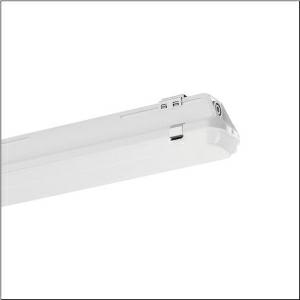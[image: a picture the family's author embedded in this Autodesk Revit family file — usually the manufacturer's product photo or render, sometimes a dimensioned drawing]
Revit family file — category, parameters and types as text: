
# Revit family: monsun_11_51fp107p4b0u
name_source: partatom
category: Lighting Fixtures
units: mm (PartAtom-declared; Revit-internal decimal feet)

## family parameters
Cut with Voids When Loaded = No
Host = Face
Light Source = No
Part Type = Normal
Room Calculation Point = No
Round Connector Dimension = Use Diameter
Shared = No

## types (1)
- Monsun 11 (1 x LED, 12070 lm, 62.4 W, 4000K)
    Apparent Load = 62 VA
    CIE Flux Codes = 47 76 93 94 100
    Color Rendering = 80
    Color Temperature = 4000K
    Default Elevation = 1800 mm
    Description = Monsun 11, damp-proof luminaire, chain hanger, primary optical cover: enclosure, of PMMA, light emission: direct distribution, primary light characteristic: symmetric, installation type: suspended mounting, surface-mounted, horizontal mounting, vertical mounting, LED, rated luminous flux: 12.070lm, luminous efficacy: 193lm/W, light colour: 840, colour temperature: 4000K, control gear: ON/OFF, with terminal, 3-pole, max. 2.5mm², mains connection: 220..240V, AC, 50/60Hz, rated input power: 62W, luminaire housing, of glass-fibre reinforced polyester, uncoated, bright grey, incl. chain hanger, length: 1.590mm, width: 90mm, height: 88mm, clip for enclosure, of stainless steel (V2A), ceiling mounting element, of stainless steel (V2A), chain hanger, of stainless steel (V2A), protection rating (complete): IP66, insulation class (complete): insulation class I (protective earthing), certification: CE, ENEC, VDE, UKCA, protection symbol: D, impact resistance: IK04, permissible operating ambient temperature: -35..+35°C, standard: EN 50419, EN 60598-2-1, contact your sales advisor before using the luminaires in applications with unclear chemical exposure, large temperature fluctuations or condensation-forming humidity, LABS conformity tested according to VDMA 24364:2018-05, no direct snow, no direct sun, no direct rain, for indoor or canopied outdoor use, corresponds to IFS (International Featured Standards) requirements for safety and quality in the food industry, packaging unit: 1 piece
    Height = 89 mm
    Lamp = 1 x LED
    Lamp Light Flux = 12070 lm
    Lamp Power = 62.4 W
    Lamp count = 1
    Length = 1590 mm
    Luminous efficacy = 193 lm/W
    Manufacturer = Siteco
    ModVariant = No
    Model = 51FP107P4B0U
    Mounting Place = Ceiling
    Mounting Type = Surface mounted
    Number of Poles = 1
    OnlyDefault = Yes
    Power Factor = 1
    Product Name = Monsun 11
    Product group = damp-proof luminaire
    ProductGroupID = 300
    Protection Class = Protection class I
    Protection Degree = IP 66
    RLX_Detail_Level = 1
    RLX_Emergency_Light_Flux = 0 lm
    RLX_Emergency_Type = 0
    RLX_Emergency_Type_DB = No
    RlxData = <blob elided: 88389 chars, md5=6763c442>
    Socket = socket
    Standby Power = 0 W
    System Light Flux = 12070 lm
    System Power = 62 W
    Type Comments = Product without accessories
    Type Image = l_1349237.jpg
    URL = http://relux.com
    VarID = ---
    Voltage = 0 V
    Weight = 0.00 kg
    Width = 90 mm

## geometry (parser evidence)
native form markers: Blend x4, Sweep x12
no freeform markers — native parametric forms only
